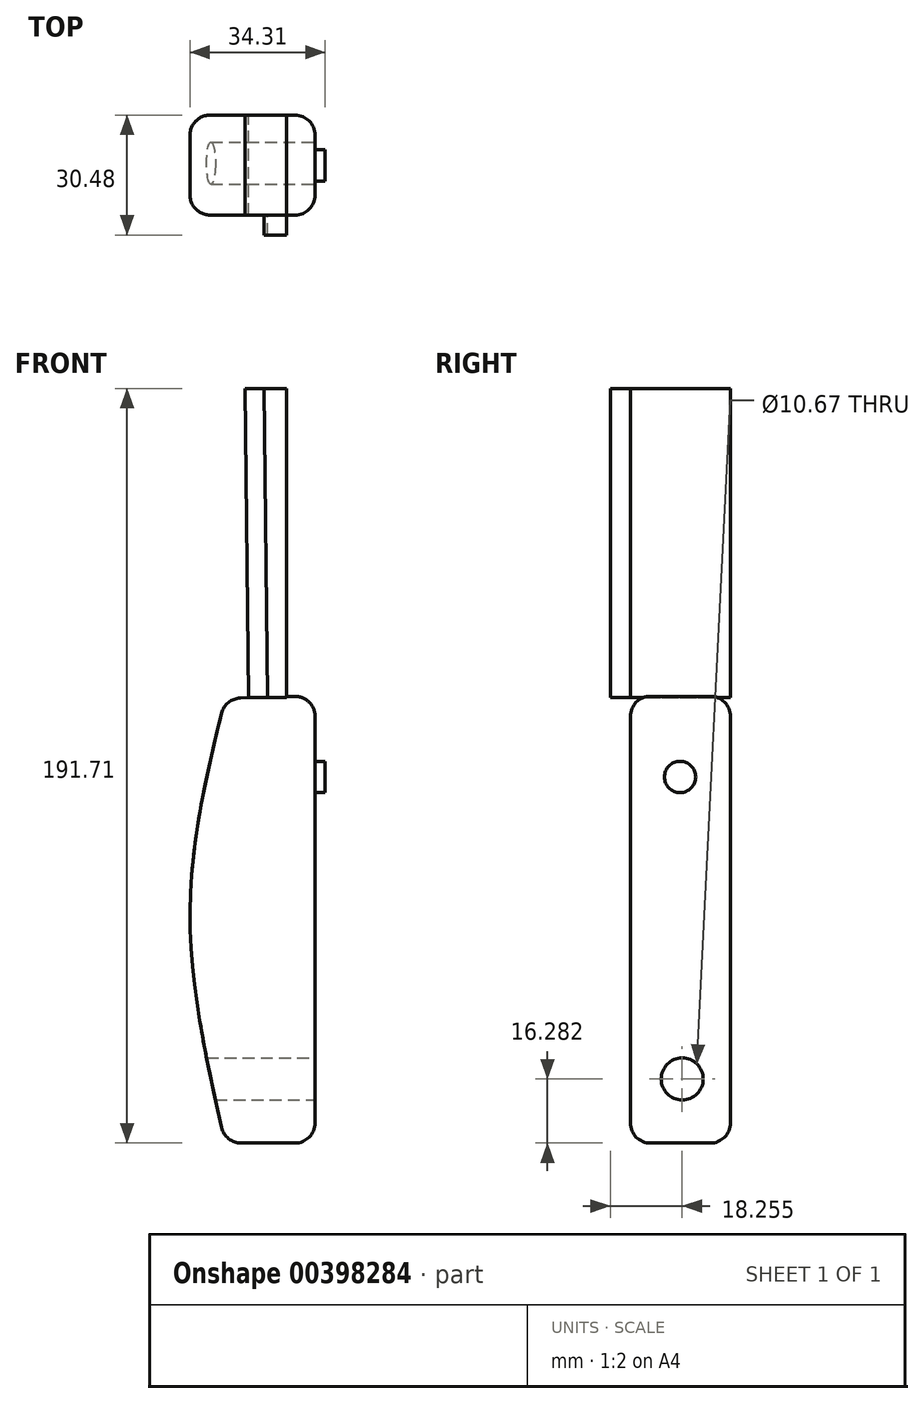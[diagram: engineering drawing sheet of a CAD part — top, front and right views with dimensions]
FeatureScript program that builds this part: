
annotation { "Feature Type Name" : "Feature", "Feature Type Description" : "" }
export const myFeature = defineFeature(function(context is Context, id is Id, definition is map)
    precondition{}
    {
        {
            var Q0;
            Q0=qCreatedBy(makeId("Front.planeOp"),FACE);
            var sketch = newSketch(context, id + "F0", { "sketchPlane" : qUnion([Q0])});
            skLineSegment(sketch, "E0", {"start": v(28.7, 58.6) * mm, "end": v(28.7, -55.07) * mm});
            skLineSegment(sketch, "E1", {"start": v(28.7, -55.07) * mm, "end": v(5.88, -55.07) * mm});
            skFitSpline(sketch, "E2", {"points": [v(5.88, -55.07) * mm, v(-3.06, 3.77) * mm, v(5.88, 57.89) * mm], "startDerivative": vector(-26.66, 116.55) * mm, "endDerivative": vector(27.02, 109.31) * mm});
            skLineSegment(sketch, "E3", {"start": v(5.88, 57.89) * mm, "end": v(28.7, 58.6) * mm});
            skSolve(sketch);
        }
        {
            var Q0;
            Q0=makeQuery(id+"F0.imprint","IMPRINT",FACE,{"disambiguationData":[TD([[makeQuery(id+"F0.imprint","IMPRINT",EDGE,{"derivedFrom":sQuery(id+"F0.wireOp",EDGE,"E0")}),-1.0]])]});
            extrude(context, id + "F1", {"entities" : qUnion([Q0]), "depth" : 25.4 * mm});
        }
        {
            var Q0;
            Q0=qCreatedBy(makeId("Front.planeOp"),FACE);
            var sketch = newSketch(context, id + "F2", { "sketchPlane" : qUnion([Q0])});
            skLineSegment(sketch, "E4", {"start": v(11.88, 58.15) * mm, "end": v(21.4, 58.15) * mm});
            skLineSegment(sketch, "E5", {"start": v(21.4, 58.15) * mm, "end": v(21.4, 136.64) * mm});
            skLineSegment(sketch, "E6", {"start": v(21.4, 136.64) * mm, "end": v(10.96, 136.64) * mm});
            skLineSegment(sketch, "E7", {"start": v(10.96, 136.64) * mm, "end": v(11.88, 58.15) * mm});
            skSolve(sketch);
        }
        {
            var Q0;
            Q0=makeQuery(id+"F2.imprint","IMPRINT",FACE,{"disambiguationData":[TD([[makeQuery(id+"F2.imprint","IMPRINT",EDGE,{"derivedFrom":sQuery(id+"F2.wireOp",EDGE,"E4")}),1.0]])]});
            extrude(context, id + "F3", {"entities" : qUnion([Q0]), "depth" : 25.4 * mm});
        }
        {
            var Q0;
            Q0=makeQuery(id+"F3.opExtrude","CAP_FACE",FACE,{"disambiguationData":[OSD([sQuery(id+"F2.wireOp",EDGE,"E4"),sQuery(id+"F2.wireOp",EDGE,"E5"),sQuery(id+"F2.wireOp",EDGE,"E6"),sQuery(id+"F2.wireOp",EDGE,"E7")])],"isStart":false});
            var sketch = newSketch(context, id + "F4", { "sketchPlane" : qUnion([Q0])});
            skLineSegment(sketch, "E8", {"start": v(16.64, 58.15) * mm, "end": v(15.73, 136.64) * mm});
            skLineSegment(sketch, "E9", {"start": v(15.73, 136.64) * mm, "end": v(21.4, 136.64) * mm});
            skLineSegment(sketch, "E10", {"start": v(21.4, 136.64) * mm, "end": v(21.4, 58.15) * mm});
            skLineSegment(sketch, "E11", {"start": v(21.4, 58.15) * mm, "end": v(16.64, 58.15) * mm});
            skSolve(sketch);
        }
        {
            var Q0;
            Q0=makeQuery(id+"F4.imprint","IMPRINT",FACE,{"disambiguationData":[TD([[makeQuery(id+"F4.imprint","IMPRINT",EDGE,{"derivedFrom":sQuery(id+"F4.wireOp",EDGE,"S7RAS3Z3-dxdY-JYj2-lJRs-eCYCP0heOCPf")}),1.0]])]});
            var Q1;
            Q1=makeQuery(id+"F4.imprint","IMPRINT",FACE,{"disambiguationData":[TD([[makeQuery(id+"F4.imprint","IMPRINT",EDGE,{"derivedFrom":sQuery(id+"F4.wireOp",EDGE,"E8")}),-1.0]])]});
            extrude(context, id + "F5", {"entities" : qUnion([Q0, Q1]), "depth" : 5.08 * mm});
        }
        {
            var Q0;
            Q0=makeQuery(id+"F1.opExtrude","CAP_EDGE",EDGE,{"disambiguationData":[OSD([sQuery(id+"F0.wireOp",EDGE,"E0")])],"isStart":true});
            var Q1;
            Q1=makeQuery(id+"F1.opExtrude","CAP_EDGE",EDGE,{"disambiguationData":[OSD([sQuery(id+"F0.wireOp",EDGE,"E0")])],"isStart":false});
            fillet(context, id + "F6", {"entities" : qUnion([Q0, Q1]), "radius" : 5.08 * mm, "tangentPropagation" : true, "allowEdgeOverflow" : false});
        }
        {
            var Q0;
            Q0=makeQuery(id+"F1.opExtrude","SWEPT_FACE",FACE,{"disambiguationData":[OSD([sQuery(id+"F0.wireOp",EDGE,"E0")])]});
            var sketch = newSketch(context, id + "F7", { "sketchPlane" : qUnion([Q0])});
            skCircle(sketch, "E12", {"center": v(-12.76, 37.96) * mm, "radius": 3.98 * mm});
            skSolve(sketch);
        }
        {
            var Q0;
            Q0=makeQuery(id+"F7.imprint","IMPRINT",FACE,{"disambiguationData":[TD([[makeQuery(id+"F7.imprint","IMPRINT",EDGE,{"derivedFrom":sQuery(id+"F7.wireOp",EDGE,"E12")}),1.0]])]});
            extrude(context, id + "F8", {"entities" : qUnion([Q0]), "operationType" : NewBodyOperationType.ADD, "depth" : 2.54 * mm});
        }
        {
            var Q0;
            Q0=makeQuery(id+"F1.opExtrude","SWEPT_FACE",FACE,{"disambiguationData":[OSD([sQuery(id+"F0.wireOp",EDGE,"E0")])]});
            var sketch = newSketch(context, id + "F9", { "sketchPlane" : qUnion([Q0])});
            skCircle(sketch, "E13", {"center": v(-12.23, -38.79) * mm, "radius": 5.33 * mm});
            skSolve(sketch);
        }
        {
            var Q0;
            Q0=makeQuery(id+"F9.imprint","IMPRINT",FACE,{"disambiguationData":[TD([[makeQuery(id+"F9.imprint","IMPRINT",EDGE,{"derivedFrom":sQuery(id+"F9.wireOp",EDGE,"E13")}),1.0]])]});
            extrude(context, id + "F10", {"entities" : qUnion([Q0]), "operationType" : NewBodyOperationType.REMOVE, "oppositeDirection" : true, "depth" : 127 * mm});
        }
        {
            var Q0;
            Q0=makeQuery(id+"F1.opExtrude","CAP_EDGE",EDGE,{"disambiguationData":[OSD([sQuery(id+"F0.wireOp",EDGE,"E2")])],"isStart":true});
            var Q1;
            Q1=makeQuery(id+"F1.opExtrude","CAP_EDGE",EDGE,{"disambiguationData":[OSD([sQuery(id+"F0.wireOp",EDGE,"E2")])],"isStart":false});
            fillet(context, id + "F11", {"entities" : qUnion([Q0, Q1]), "radius" : 5.08 * mm, "tangentPropagation" : true, "allowEdgeOverflow" : false});
        }
        {
            var Q0;
            Q0=makeQuery(id+"F1.opExtrude","CAP_FACE",FACE,{"disambiguationData":[OSD([sQuery(id+"F0.wireOp",EDGE,"E0"),sQuery(id+"F0.wireOp",EDGE,"E1"),sQuery(id+"F0.wireOp",EDGE,"E2"),sQuery(id+"F0.wireOp",EDGE,"E3")])],"isStart":true});
            var Q1;
            Q1=makeQuery(id+"F1.opExtrude","CAP_FACE",FACE,{"disambiguationData":[OSD([sQuery(id+"F0.wireOp",EDGE,"E0"),sQuery(id+"F0.wireOp",EDGE,"E1"),sQuery(id+"F0.wireOp",EDGE,"E2"),sQuery(id+"F0.wireOp",EDGE,"E3")])],"isStart":false});
            fillet(context, id + "F12", {"entities" : qUnion([Q0, Q1]), "radius" : 5.08 * mm, "tangentPropagation" : true, "allowEdgeOverflow" : false});
        }
    });
